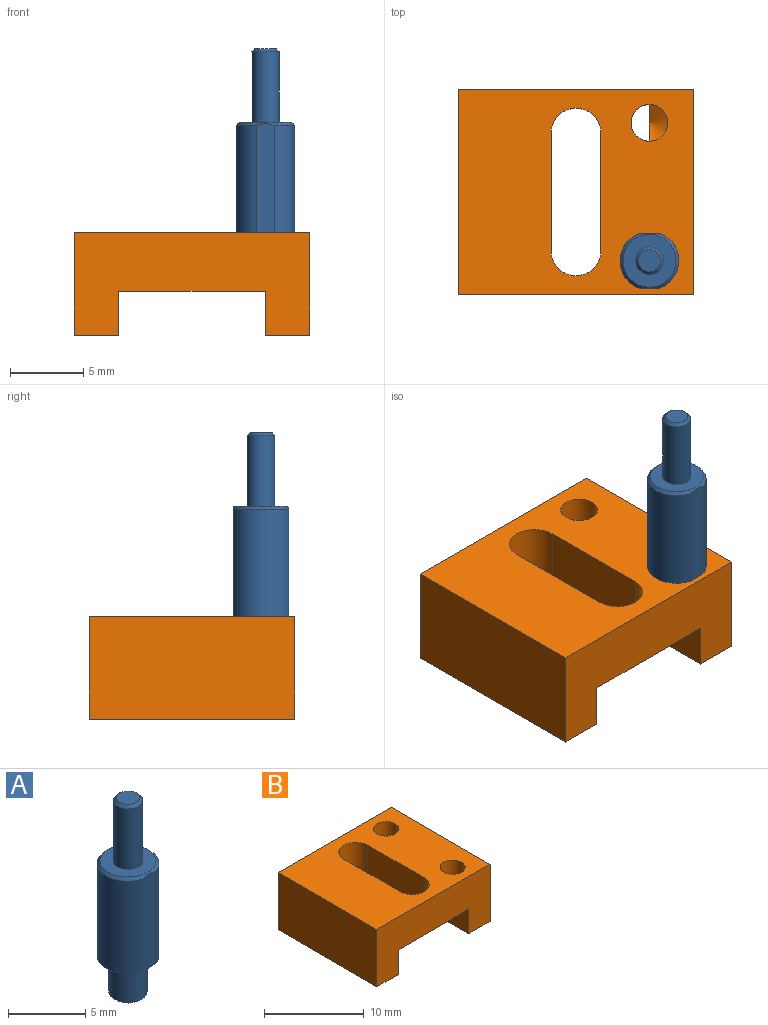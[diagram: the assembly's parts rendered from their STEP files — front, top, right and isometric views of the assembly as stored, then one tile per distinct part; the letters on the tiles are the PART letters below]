
ASSEMBLY  parts=2 mates=1
PART A: 13 faces, bbox 4x4x15.5 mm
  f0: cylinder r=2mm len=7.3mm, axis (0,0,-1), area 35.5mm2, adj f2,f3,f11,f12
  f1: cylinder r=2mm len=7.3mm, axis (0,0,-1), area 35.5mm2, adj f2,f3,f11,f12
  f2: plane 4x3.75mm, normal (0,0,-1), area 7.4mm2, adj f0,f1,f5,f11,f12
  f3: cone r=1.8mm half-angle=45deg, axis (0,0,-1), area 3mm2, adj f0,f1,f4,f11,f12
  f4: plane 3.6x3.6mm, normal (0,0,1), area 7.3mm2, adj f3,f7
  f5: cylinder r=1.25mm len=2.8mm, axis (0,0,1), area 22mm2, adj f2,f10
  f6: plane 2.1x2.1mm, normal (0,0,-1), area 3.5mm2, adj f10
  f7: cylinder r=0.95mm len=4.8mm, axis (0,0,-1), area 28.7mm2, adj f4,f9
  f8: plane 1.5x1.5mm, normal (0,0,1), area 1.8mm2, adj f9
  f9: cone r=0.75mm half-angle=45deg, axis (0,0,-1), area 1.5mm2, adj f7,f8
  f10: cone r=1.25mm half-angle=45deg, axis (0,0,1), area 2mm2, adj f5,f6
  f11: plane 7.4x1.25mm, normal (0,-1,0), area 9.2mm2, adj f0,f1,f2,f3
  f12: plane 7.45x1.52mm, normal (0,1,0), area 11.2mm2, adj f0,f1,f2,f3
PART B: 18 faces, bbox 16x14x7 mm
  f0: plane 14x3mm, normal (-1,0,0), area 40.1mm2, adj f6,f7,f8,f9,f10,f12
  f1: plane 14x3mm, normal (1,0,0), area 42mm2, adj f2,f7,f8,f9
  f2: plane 14x3mm, normal (0,0,-1), area 42mm2, adj f1,f3,f8,f9
  f3: plane 14x7mm, normal (-1,0,0), area 98mm2, adj f2,f4,f8,f9
  f4: plane 16x14mm, normal (0,0,1), area 177.9mm2, adj f3,f5,f8,f9,f11,f13,f14,f15
  f5: plane 14x7mm, normal (1,0,0), area 98mm2, adj f4,f6,f8,f9
  f6: plane 14x3mm, normal (0,0,-1), area 42mm2, adj f0,f5,f8,f9
  f7: plane 14x10mm, normal (0,0,-1), area 98.8mm2, adj f0,f1,f8,f9,f11,f13,f14,f15
  f8: plane 16x7mm, normal (0,1,0), area 82mm2, adj f0,f1,f2,f3,f4,f5,f6,f7
  f9: plane 16x7mm, normal (0,-1,0), area 82mm2, adj f0,f1,f2,f3,f4,f5,f6,f7
  f10: cone r=0mm half-angle=59deg, axis (0,0,1), area 2.9mm2, adj f0,f11
  f11: cylinder r=1.25mm len=4mm, axis (0,0,1), area 31.4mm2, adj f4,f7,f10
  f12: cone r=0mm half-angle=59deg, axis (0,0,1), area 2.9mm2, adj f0,f13
  f13: cylinder r=1.25mm len=4mm, axis (0,0,1), area 31.4mm2, adj f4,f7,f12
  f14: plane 8x4mm, normal (1,0,0), area 32mm2, adj f4,f7,f15,f17
  f15: cylinder r=1.7mm len=4mm, axis (0,0,1), area 21.4mm2, adj f4,f7,f14,f16
  f16: plane 8x4mm, normal (-1,0,0), area 32mm2, adj f4,f7,f15,f17
  f17: cylinder r=1.7mm len=4mm, axis (0,0,1), area 21.4mm2, adj f4,f7,f14,f16
PLACE A t=(55.26,-50.2,-18.64)mm
PLACE B t=(55.26,-40.8,-18.64)mm
MATE fastened A.f0 <-> B.f10  axis (0,0,-1) through (175.2,13.77,-1.14)mm
